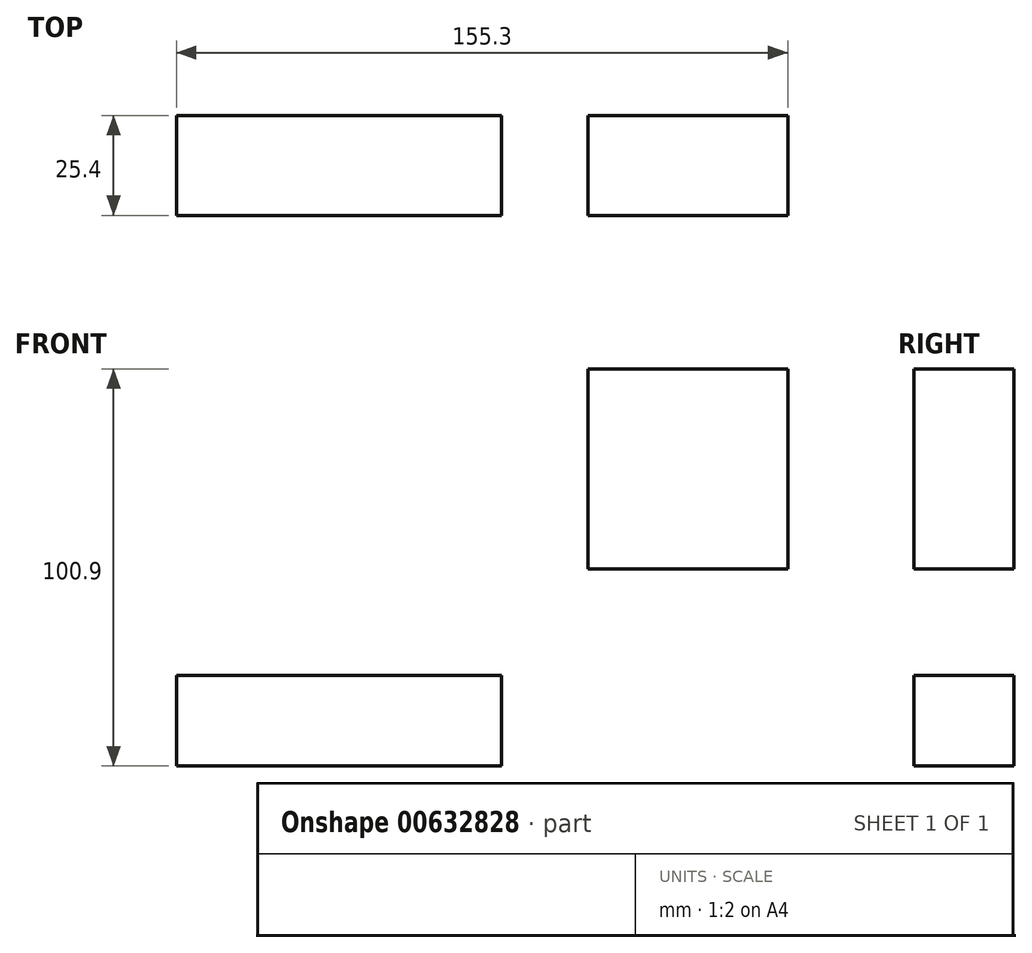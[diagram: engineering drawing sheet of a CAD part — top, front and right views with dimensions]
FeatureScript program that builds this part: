
annotation { "Feature Type Name" : "Feature", "Feature Type Description" : "" }
export const myFeature = defineFeature(function(context is Context, id is Id, definition is map)
    precondition{}
    {
        {
            var Q0;
            Q0=qCreatedBy(makeId("Front.planeOp"),FACE);
            var sketch = newSketch(context, id + "F0", { "sketchPlane" : qUnion([Q0])});
            skLineSegment(sketch, "E0.bottom", {"start": v(-41.28, 11.52) * mm, "end": v(41.28, 11.52) * mm});
            skLineSegment(sketch, "E0.top", {"start": v(-41.28, -11.52) * mm, "end": v(41.28, -11.52) * mm});
            skLineSegment(sketch, "E0.left", {"start": v(-41.28, 11.52) * mm, "end": v(-41.28, -11.52) * mm});
            skLineSegment(sketch, "E0.right", {"start": v(41.28, 11.52) * mm, "end": v(41.28, -11.52) * mm});
            skPoint(sketch, "E0.middle", {"position": v(0, 0) * mm});
            skLineSegment(sketch, "E1.bottom", {"start": v(63.23, 38.58) * mm, "end": v(114.03, 38.58) * mm});
            skLineSegment(sketch, "E1.top", {"start": v(63.23, 89.38) * mm, "end": v(114.03, 89.38) * mm});
            skLineSegment(sketch, "E1.left", {"start": v(63.23, 38.58) * mm, "end": v(63.23, 89.38) * mm});
            skLineSegment(sketch, "E1.right", {"start": v(114.03, 38.58) * mm, "end": v(114.03, 89.38) * mm});
            skPoint(sketch, "E1.middle", {"position": v(88.63, 63.98) * mm});
            skLineSegment(sketch, "E2", {"start": v(41.28, 11.52) * mm, "end": v(41.28, 30.84) * mm});
            skArc(sketch, "E3", {"start": v(41.27, 30.84) * mm, "mid": v(45.92, 42.06) * mm, "end": v(57.15, 46.71) * mm});
            skLineSegment(sketch, "E4", {"start": v(57.15, 46.71) * mm, "end": v(85.55, 46.71) * mm});
            skSolve(sketch);
        }
        {
            var Q0;
            Q0 = qSketchRegion(id + "F0", true);
            extrude(context, id + "F1", {"entities" : qUnion([Q0]), "depth" : 25.4 * mm, "offsetDistance" : 25.4 * mm});
        }
    });
